# Revit family: IS_TonicII_R4357_BIM_DE
name_source: partatom
category: Plumbing Fixtures
revit_build: Autodesk Revit MEP 2016 (Build: 20161004_0715(x64)
units: mm (PartAtom-declared; Revit-internal decimal feet)

## family parameters
Always vertical = No
Cut with Voids When Loaded = No
OmniClass Number = 23.45.05.14.17.11
OmniClass Title = Shower Compartments
Part Type = Normal
Room Calculation Point = No
Round Connector Dimension = Use Diameter
Shared = No
Work Plane-Based = No

## types (2) — shared parameters
Accessories = www.idealstandard.de\ersatzteile
AreaUnits = millimeters
AssetType = Fixed
BIMobject category = Accessories
BOSUseNativeGeometries = 1
Brand = Ideal Standard
Brand url = http://www.idealstandard.co.uk
ConnectionType = Mechanical
CurrencyUnit = €
Date of publishing = 06/11/2017
DurationUnit = year
Edition number = 1
ExpectedLife = 25
Features = TONIC II furniture handle for vanity unit 497x66mm
IFC Classification = Sanitary Terminal
IfcExportAs = Sanitary Terminal Type
IfcExportType = SupportRails
Installation instructions = http://www.idealstandard.de
InstallationInstructions = www.idealstandard.de\produkte
LinearUnits = millimeters
MaintenanceInformation = www.idealstandard.de\produkte
Manufacturer name = Ideal Standard
ManufacturerURL = www.idealstandard.com
ModelReference = TONIC II furniture handle for vanity unit 497x66mm
NBS Reference Code = 85-85
NBS Reference Description = Support Rails
NettWeight = 0,51 kg
Nominal height = 30
Nominal width = 497
NominalDepth = 66 mm  [stored 0.216535 ft]
NominalHeight = 30 mm  [stored 0.0984252 ft]
NominalLength = 66 mm  [stored 0.216535 ft]
NominalWidth = 497 mm  [stored 1.63058 ft]
OmniClass Code = 23-31 25 00
OmniClass Description = Toilet and Bath Specialties
Product Guid = 0e0bd8d7-2d98-4932-a091-b009fed88495
Product SKU = R4357
Product data url = https://bimobject.com
Product family = TONIC II
Product group = Accessories
Product name = TONIC II furniture handle for vanity unit 497x66mm
Product url = http://www.idealstandard.de
ProductInformation = www.idealstandard.de/produkte
QR code = http://bimobject.com
Shape = Sculptured
Size = 30 x 66 x 497mm
Space = Internal
SpareParts = www.idealstandard.de/ersatzteile
Technical description = http://www.idealstandard.de
URL = www.idealstandard.com
Uniclass 1.4 Code = L2132
Uniclass 1.4 Description = Rails
Uniclass 2.0 Code = PR-85-85
Uniclass 2.0 Description = Support Rails
Uniclass 2015 Code = Pr_40_20_76_84
Uniclass 2015 Name = Support rails
Uniclass2015Code = Pr_40_20_76_84
Uniclass2015Title = Support rails
Uniclass2015Version = Products v1.1
Version = 1
VolumeUnits = Litres
Weight Net (Kg) = 0.51

## per-type parameters (varying)
| type | BIMObjectName | BarCode | Color | Description | EAN code | Finish | MainColor | Model | ModelNumber | Name |
| R4357AA - TONIC II furniture handle for vanity unit 497x66mm | ISI_IdealStandard_Furniture_Tonic Ii_R4357AA | 3391500572522 | Chrome | R4357AA TONIC II furniture handle for vanity unit 497x66mm | https://3391500572522 | Chrome | Chrome | R4357AA | R4357AA | Furniture_Tonic Ii_R4357AA_IdealStandard |
| R4357WG - TONIC II furniture handle for vanity unit 497x66mm | ISI_IdealStandard_Furniture_Tonic Ii_R4357WG | 3391500572515 | Glossy White | R4357WG TONIC II furniture handle for vanity unit 497x66mm | https://3391500572515 | Glossy White | Glossy White | R4357WG | R4357WG | Furniture_Tonic Ii_R4357WG_IdealStandard |

note: [stored X ft] marks values corroborated as IEEE doubles in the binary element streams (Revit-internal decimal feet)

## geometry (parser evidence)
native form markers: Blend x2, Sweep x3
no freeform markers — native parametric forms only
